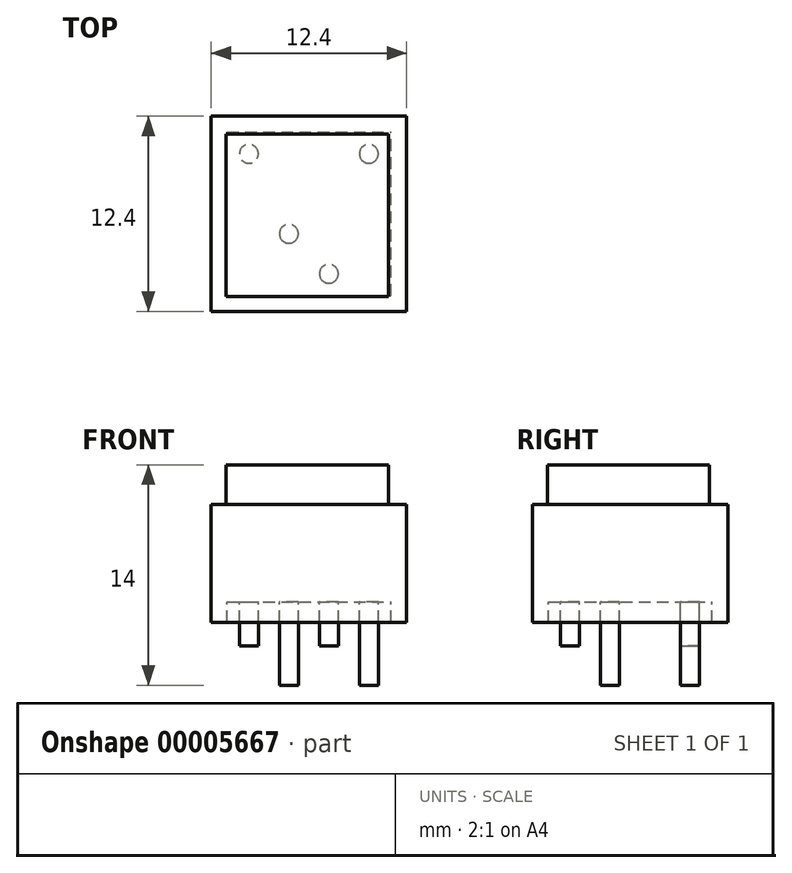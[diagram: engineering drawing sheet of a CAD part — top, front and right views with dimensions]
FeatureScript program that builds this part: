
annotation { "Feature Type Name" : "Feature", "Feature Type Description" : "" }
export const myFeature = defineFeature(function(context is Context, id is Id, definition is map)
    precondition{}
    {
        {
            var Q0;
            Q0=qCreatedBy(makeId("Top.planeOp"),FACE);
            var sketch = newSketch(context, id + "F0", { "sketchPlane" : qUnion([Q0])});
            skLineSegment(sketch, "E0.bottom", {"start": v(0, 0) * mm, "end": v(12.4, 0) * mm});
            skLineSegment(sketch, "E0.top", {"start": v(0, -12.4) * mm, "end": v(12.4, -12.4) * mm});
            skLineSegment(sketch, "E0.left", {"start": v(0, 0) * mm, "end": v(0, -12.4) * mm});
            skLineSegment(sketch, "E0.right", {"start": v(12.4, 0) * mm, "end": v(12.4, -12.4) * mm});
            skSolve(sketch);
        }
        {
            var Q0;
            Q0=makeQuery(id+"F0.imprint","IMPRINT",FACE,{"disambiguationData":[TD([[makeQuery(id+"F0.imprint","IMPRINT",EDGE,{"derivedFrom":sQuery(id+"F0.wireOp",EDGE,"E0.bottom")}),-1.0]])]});
            extrude(context, id + "F1", {"entities" : qUnion([Q0]), "depth" : 6.2 * mm});
        }
        {
            var Q0;
            Q0=makeQuery(id+"F1.opExtrude","CAP_FACE",FACE,{"disambiguationData":[OSD([sQuery(id+"F0.wireOp",EDGE,"E0.bottom"),sQuery(id+"F0.wireOp",EDGE,"E0.top"),sQuery(id+"F0.wireOp",EDGE,"E0.left"),sQuery(id+"F0.wireOp",EDGE,"E0.right")])],"isStart":true});
            var sketch = newSketch(context, id + "F2", { "sketchPlane" : qUnion([Q0])});
            skLineSegment(sketch, "E1.bottom", {"start": v(0, 12.4) * mm, "end": v(12.4, 12.4) * mm});
            skLineSegment(sketch, "E1.top", {"start": v(0, 0) * mm, "end": v(12.4, 0) * mm});
            skLineSegment(sketch, "E1.left", {"start": v(0, 12.4) * mm, "end": v(0, 0) * mm});
            skLineSegment(sketch, "E1.right", {"start": v(12.4, 12.4) * mm, "end": v(12.4, 0) * mm});
            skLineSegment(sketch, "E2.bottom", {"start": v(1, 11.4) * mm, "end": v(11.4, 11.4) * mm});
            skLineSegment(sketch, "E2.top", {"start": v(1, 1) * mm, "end": v(11.4, 1) * mm});
            skLineSegment(sketch, "E2.left", {"start": v(1, 11.4) * mm, "end": v(1, 1) * mm});
            skLineSegment(sketch, "E2.right", {"start": v(11.4, 11.4) * mm, "end": v(11.4, 1) * mm});
            skSolve(sketch);
        }
        {
            var Q0;
            Q0=makeQuery(id+"F1.opExtrude","CAP_FACE",FACE,{"disambiguationData":[OSD([sQuery(id+"F0.wireOp",EDGE,"E0.bottom"),sQuery(id+"F0.wireOp",EDGE,"E0.top"),sQuery(id+"F0.wireOp",EDGE,"E0.left"),sQuery(id+"F0.wireOp",EDGE,"E0.right")])],"isStart":false});
            var sketch = newSketch(context, id + "F3", { "sketchPlane" : qUnion([Q0])});
            skLineSegment(sketch, "E3.bottom", {"start": v(0.95, -1.15) * mm, "end": v(11.25, -1.15) * mm});
            skLineSegment(sketch, "E3.top", {"start": v(0.95, -11.45) * mm, "end": v(11.25, -11.45) * mm});
            skLineSegment(sketch, "E3.left", {"start": v(0.95, -1.15) * mm, "end": v(0.95, -11.45) * mm});
            skLineSegment(sketch, "E3.right", {"start": v(11.25, -1.15) * mm, "end": v(11.25, -11.45) * mm});
            skSolve(sketch);
        }
        {
            var Q0;
            Q0 = qSketchRegion(id + "F3", true);
            extrude(context, id + "F4", {"entities" : qUnion([Q0]), "depth" : 2.5 * mm});
        }
        {
            var Q0;
            Q0=makeQuery(id+"F1.opExtrude","CAP_FACE",FACE,{"disambiguationData":[OSD([sQuery(id+"F0.wireOp",EDGE,"E0.bottom"),sQuery(id+"F0.wireOp",EDGE,"E0.top"),sQuery(id+"F0.wireOp",EDGE,"E0.left"),sQuery(id+"F0.wireOp",EDGE,"E0.right")])],"isStart":true});
            var sketch = newSketch(context, id + "F5", { "sketchPlane" : qUnion([Q0])});
            skCircle(sketch, "E4", {"center": v(2.4, 2.39) * mm, "radius": 0.6 * mm});
            skSolve(sketch);
        }
        {
            var Q0;
            Q0 = qSketchRegion(id + "F5", true);
            extrude(context, id + "F6", {"entities" : qUnion([Q0]), "operationType" : NewBodyOperationType.ADD, "depth" : 2.8 * mm});
        }
        {
            var Q0;
            Q0=makeQuery(id+"F1.opExtrude","CAP_FACE",FACE,{"disambiguationData":[OSD([sQuery(id+"F0.wireOp",EDGE,"E0.bottom"),sQuery(id+"F0.wireOp",EDGE,"E0.top"),sQuery(id+"F0.wireOp",EDGE,"E0.left"),sQuery(id+"F0.wireOp",EDGE,"E0.right")])],"isStart":true});
            var sketch = newSketch(context, id + "F7", { "sketchPlane" : qUnion([Q0])});
            skCircle(sketch, "E5", {"center": v(7.47, 10) * mm, "radius": 0.6 * mm});
            skSolve(sketch);
        }
        {
            var Q0;
            Q0 = qSketchRegion(id + "F7", true);
            extrude(context, id + "F8", {"entities" : qUnion([Q0]), "operationType" : NewBodyOperationType.ADD, "depth" : 2.8 * mm});
        }
        {
            var Q0;
            Q0=makeQuery(id+"F1.opExtrude","CAP_FACE",FACE,{"disambiguationData":[OSD([sQuery(id+"F0.wireOp",EDGE,"E0.bottom"),sQuery(id+"F0.wireOp",EDGE,"E0.top"),sQuery(id+"F0.wireOp",EDGE,"E0.left"),sQuery(id+"F0.wireOp",EDGE,"E0.right")])],"isStart":true});
            var sketch = newSketch(context, id + "F9", { "sketchPlane" : qUnion([Q0])});
            skCircle(sketch, "E6", {"center": v(10, 2.4) * mm, "radius": 0.6 * mm});
            skSolve(sketch);
        }
        {
            var Q0;
            Q0 = qSketchRegion(id + "F9", true);
            extrude(context, id + "F10", {"entities" : qUnion([Q0]), "operationType" : NewBodyOperationType.ADD, "depth" : 5.3 * mm});
        }
        {
            var Q0;
            Q0=makeQuery(id+"F1.opExtrude","CAP_FACE",FACE,{"disambiguationData":[OSD([sQuery(id+"F0.wireOp",EDGE,"E0.bottom"),sQuery(id+"F0.wireOp",EDGE,"E0.top"),sQuery(id+"F0.wireOp",EDGE,"E0.left"),sQuery(id+"F0.wireOp",EDGE,"E0.right")])],"isStart":true});
            var sketch = newSketch(context, id + "F11", { "sketchPlane" : qUnion([Q0])});
            skCircle(sketch, "E7", {"center": v(4.93, 7.47) * mm, "radius": 0.6 * mm});
            skSolve(sketch);
        }
        {
            var Q0;
            Q0 = qSketchRegion(id + "F11", true);
            extrude(context, id + "F12", {"entities" : qUnion([Q0]), "operationType" : NewBodyOperationType.ADD, "depth" : 5.3 * mm});
        }
        {
            var Q0;
            Q0 = qSketchRegion(id + "F2", true);
            extrude(context, id + "F13", {"entities" : qUnion([Q0]), "operationType" : NewBodyOperationType.ADD, "depth" : 1.3 * mm});
        }
    });
